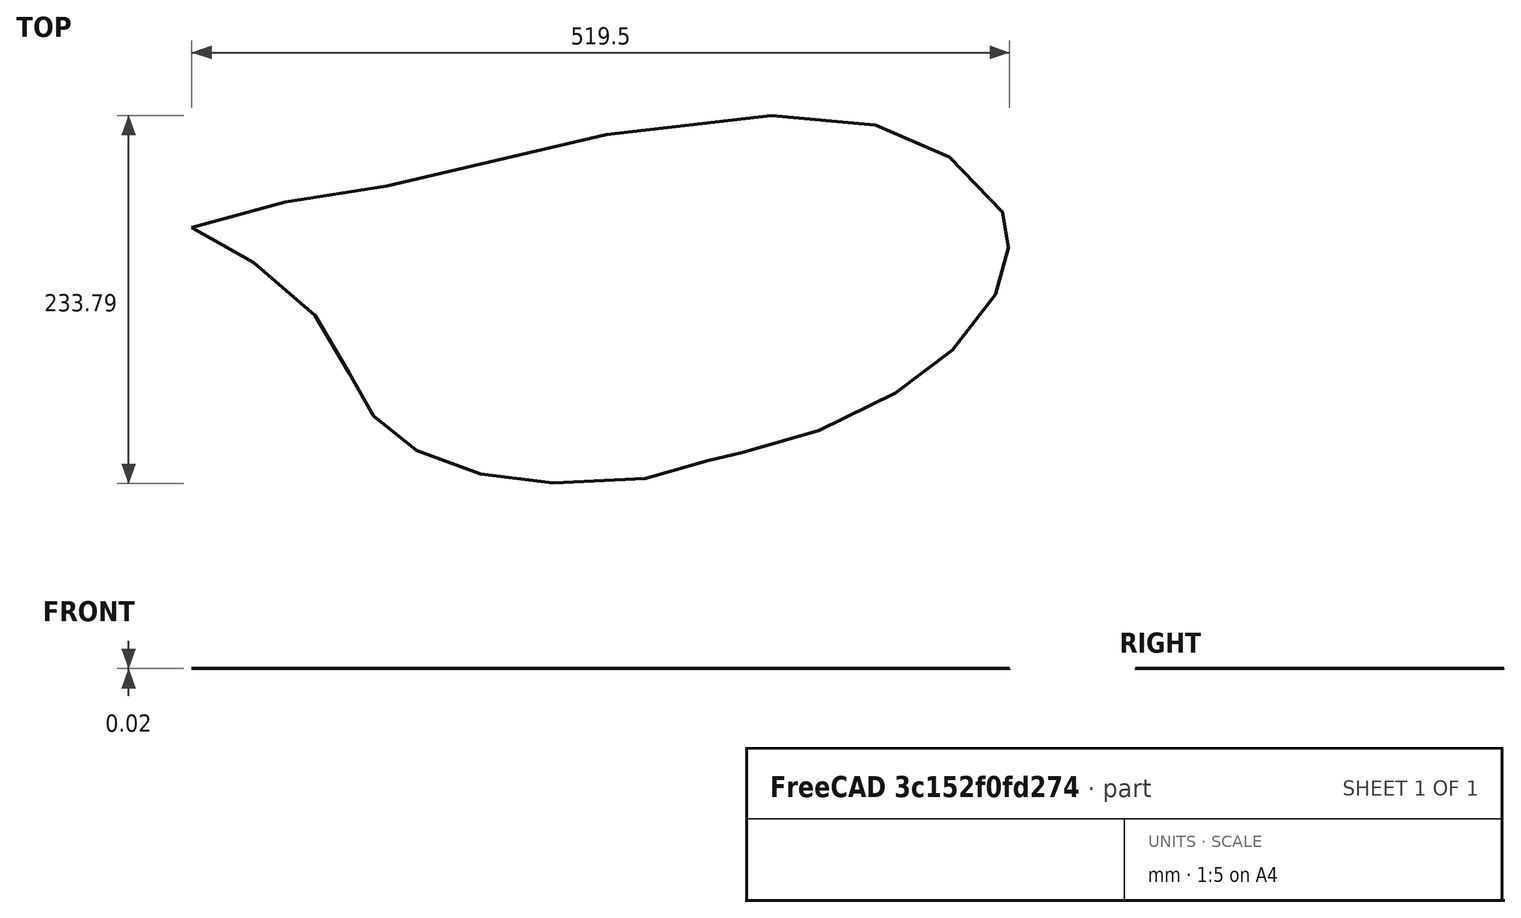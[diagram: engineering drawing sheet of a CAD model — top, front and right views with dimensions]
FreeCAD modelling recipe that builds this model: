
FCSTD DOCUMENT  (FreeCAD 0.20R29177 (Git))
Label: wing_surf
License: All rights reserved
LicenseURL: http://en.wikipedia.org/wiki/All_rights_reserved
objects: Sketcher::SketchObject×1, PartDesign::Pad×1, PartDesign::Body×1
note: 4 computed .brp shape members not serialized (recipe doc carries the construction recipe); baked Part::Feature solids carry a one-line shape summary decoded from their .brp

FEATURE [Sketcher::SketchObject] Sketch  label="WingOutlineSketch"
  FullyConstrained = false
  MapMode = 5
  Support = -> [XY_Plane]
  sketch-geometry (150):
    g0: LineSegment StartX=0 StartY=0 StartZ=0 EndX=519.07 EndY=0 EndZ=0
    g1-g75: Circle x75 (B-spline internal-alignment scaffolding for g76; pole/knot coordinates omitted)
    g76: BSplineCurve PolesCount=75 KnotsCount=73 Degree=3 IsPeriodic=0
    g77-g149: GeomPoint x73 (B-spline internal-alignment scaffolding for g76; pole/knot coordinates omitted)
  constraints (11):
    c: Horizontal(g0)
    c: Coincident(g0,g-1)
    c: Weight(g1) = 1
    c: Coincident(g76,g0)
    c: Equal(g1, g2-g25) x24
    c: Coincident(g25,g0)
    c: Equal(g1, g26-g75) x50
    c: Coincident(g76,g0)
    c: InternalAlignment(g1-g75 -> g76) x75
    c: InternalAlignment(g77-g149 -> g76) x73
    c: DistanceX(g0,g0) = 519.07
FEATURE [PartDesign::Pad] Pad  label="WingOutlinePad"
  Direction = (0,0,1)
  Length = 0.01
  Length2 = 10
  Midplane = true
  Profile = -> Sketch
  ReferenceAxis = -> Sketch [N_Axis]
  Type = 0
FEATURE [PartDesign::Body] Body
  Group = -> [Sketch,Pad]
  Origin = -> Origin
  Tip = -> Pad
